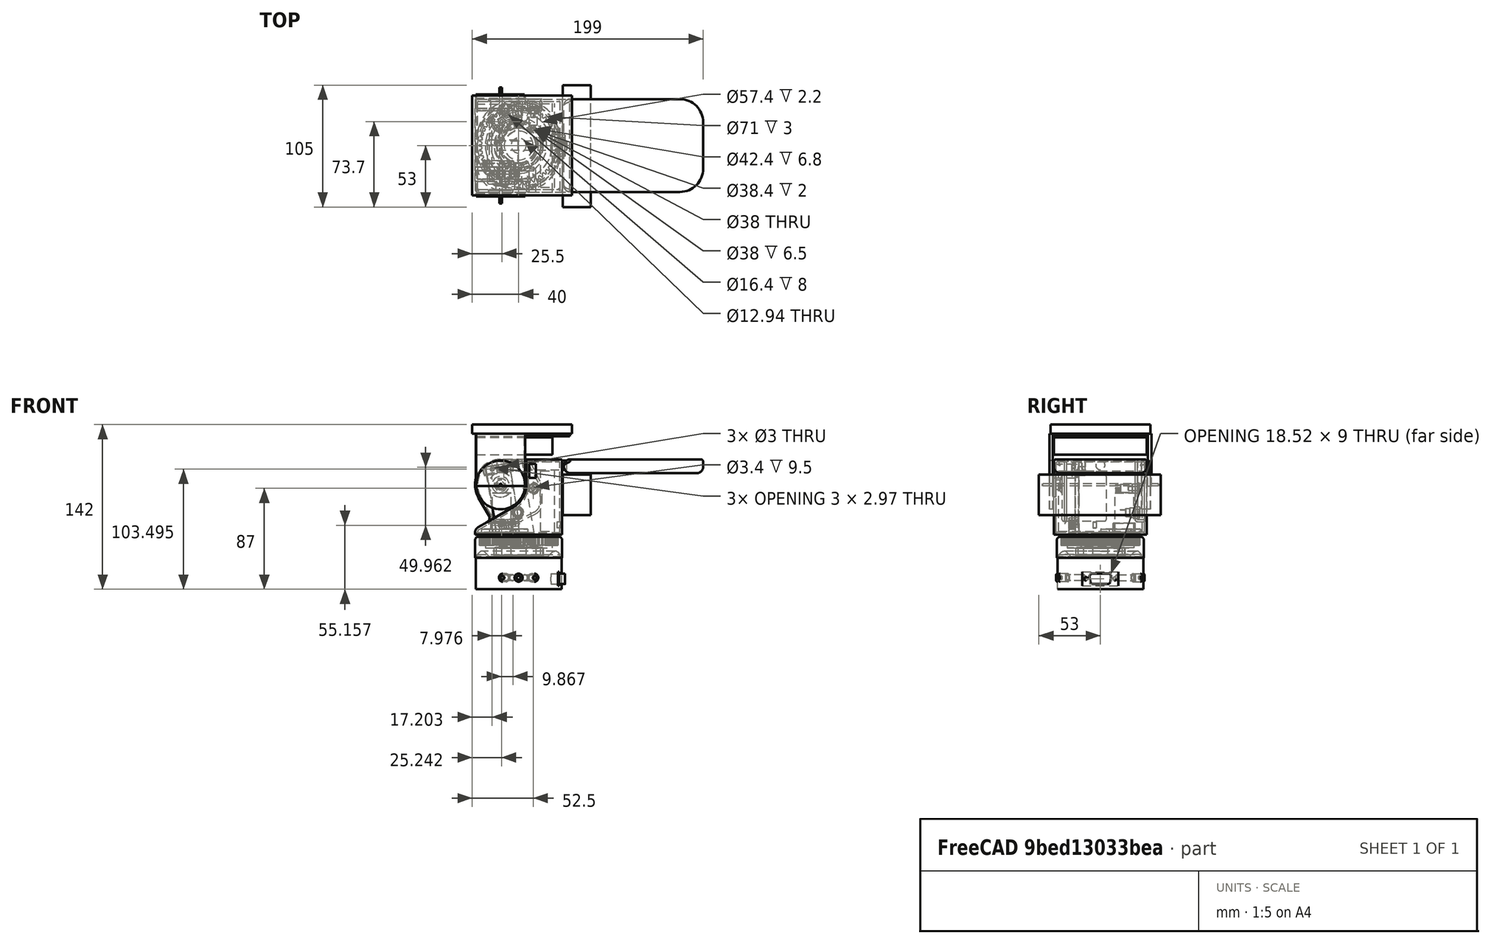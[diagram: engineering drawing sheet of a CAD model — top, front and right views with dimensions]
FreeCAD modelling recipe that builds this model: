
FCSTD DOCUMENT  (FreeCAD 0.16R6703 (Git))
Label: slewing_ring
License: CC-BY 3.0
LicenseURL: http://creativecommons.org/licenses/by/3.0/
objects: Part::Cylinder×23, Part::Fillet×23, Part::Cut×22, Part::Box×18, Part::Chamfer×8, Sketcher::SketchObject×7, Part::MultiFuse×7, Part::Sphere×4, Part::Extrusion×4, PartDesign::Fillet×4, Part::Cone×2, Part::FeaturePython×2, PartDesign::Revolution×1, Mesh::Feature×1, Part::Part2DObjectPython×1, Part::Revolution×1, Part::Feature×1, Part::Thickness×1, Part::Common×1
note: 131 computed .brp shape members not serialized (recipe doc carries the construction recipe); baked Part::Feature solids carry a one-line shape summary decoded from their .brp

FEATURE [Sketcher::SketchObject] Sketch  label="SlewingRingLowerBlankSketch"
  Placement = pos=(0,0,0) rot=(1,0,0;1.5708rad)
  sketch-geometry (13):
    g0: LineSegment StartX=-37.5 StartY=0 StartZ=0 EndX=-37.5 EndY=18.3 EndZ=0
    g1: LineSegment StartX=-37.5 StartY=18.3 StartZ=0 EndX=-28.7 EndY=18.3 EndZ=0
    g2: LineSegment StartX=-28.7 StartY=18.3 StartZ=0 EndX=-28.7 EndY=8.8 EndZ=0
    g3: LineSegment StartX=-28.7 StartY=8.8 StartZ=0 EndX=-21.2 EndY=8.8 EndZ=0
    g4: LineSegment StartX=-21.2 StartY=8.8 StartZ=0 EndX=-21.2 EndY=2 EndZ=0
    g5: LineSegment StartX=-21.2 StartY=2 StartZ=0 EndX=-19.2 EndY=2 EndZ=0
    g6: LineSegment StartX=-19.2 StartY=2 StartZ=0 EndX=-19.2 EndY=0 EndZ=0
    g7: LineSegment StartX=-37.5 StartY=0 StartZ=0 EndX=-35.5 EndY=0 EndZ=0
    g8: LineSegment StartX=-35.5 StartY=0 StartZ=0 EndX=-35.5 EndY=3 EndZ=0
    g9: LineSegment StartX=-35.5 StartY=3 StartZ=0 EndX=-33.4426 EndY=5.05736 EndZ=0
    g10: LineSegment StartX=-19.2 StartY=0 StartZ=0 EndX=-24.1426 EndY=0 EndZ=0
    g11: LineSegment StartX=-29.2 StartY=5.05736 StartZ=0 EndX=-24.1426 EndY=0 EndZ=0
    g12: ArcOfCircle CenterX=-31.3213 CenterY=2.93604 CenterZ=0 NormalX=0 NormalY=0 NormalZ=1 Radius=3 StartAngle=0.785398 EndAngle=2.35619
  constraints (38):
    c: Vertical(g0)
    c: Coincident(g0,g1)
    c: Horizontal(g1)
    c: Coincident(g1,g2)
    c: Vertical(g2)
    c: Coincident(g2,g3)
    c: Horizontal(g3)
    c: Coincident(g3,g4)
    c: Vertical(g4)
    c: Coincident(g4,g5)
    c: Coincident(g5,g6)
    c: DistanceY(g-1,g6) = 0
    c: Vertical(g6)
    c: Horizontal(g5)
    c: DistanceX(g4,g5) = 2
    c: DistanceY(g3,g4) = -6.8
    c: DistanceY(g5,g6) = -2
    c: DistanceX(g-1,g3) = -21.2
    c: DistanceX(g3,g2) = -7.5
    c: DistanceX(g-1,g0) = -37.5
    c: DistanceY(g2,g1) = 9.5
    c: DistanceY(g-1,g0) = 0
    c: Horizontal(g7)
    c: DistanceX(g7) = 2
    c: Coincident(g7,g0)
    c: Vertical(g8)
    c: DistanceY(g8) = 3
    c: Coincident(g8,g7)
    c: Angle(g9) = 0.785398
    c: Coincident(g9,g8)
    c: Horizontal(g10)
    c: Coincident(g10,g6)
    c: Coincident(g11,g10)
    c: Angle(g11) = -0.785398
    c: Distance(g2,g11) = 3
    c: Tangent(g9,g12)
    c: Tangent(g11,g12)
    c: Distance(g12,g9) = 3
FEATURE [Part::Cylinder] Cylinder  label="Cylinder21R"
  Angle = 360
  Height = 7
  Radius = 21
FEATURE [Part::Cylinder] Cylinder001  label="Cylinder19R"
  Angle = 360
  Height = 10
  Placement = pos=(0,0,-1.5) rot=(0,0,1;0rad)
  Radius = 19
FEATURE [Part::Cut] Cut  label="OuterRace"
  Base = -> Cylinder
  Tool = -> Cylinder001
FEATURE [Part::Cylinder] Cylinder002  label="Cylinder17R"
  Angle = 360
  Height = 7
  Radius = 17
FEATURE [Part::Cut] Cut001
  Base = -> Cylinder002
FEATURE [Part::Chamfer] Chamfer
  Base = -> Cut
  Edges = 1 edges r=0.5: [Edge1]
FEATURE [Part::Chamfer] Chamfer001
  Base = -> Chamfer
  Edges = 1 edges r=0.5: [Edge3]
FEATURE [Part::Chamfer] Chamfer002
  Base = -> Cut001
  Edges = 1 edges r=0.5: [Edge5]
FEATURE [Part::Chamfer] Chamfer003
  Base = -> Chamfer002
  Edges = 1 edges r=0.5: [Edge11]
FEATURE [Part::Chamfer] Chamfer004
  Base = -> Chamfer003
  Edges = 1 edges r=0.25: [Edge12]
FEATURE [Part::Chamfer] Chamfer005
  Base = -> Chamfer001
  Edges = 1 edges r=0.25: [Edge10]
FEATURE [Part::Sphere] Sphere  label="ballN"
  Angle1 = -90
  Angle2 = 90
  Angle3 = 360
  Placement = pos=(18,0,3.5) rot=(0,0,1;0rad)
  Radius = 2.5
FEATURE [Part::Sphere] Sphere3  label="ballS"
  Angle1 = -90
  Angle2 = 90
  Angle3 = 360
  Placement = pos=(-18,0,3.5) rot=(0,0,1;0rad)
  Radius = 2.5
FEATURE [Part::Sphere] Sphere004  label="ballW"
  Angle1 = -90
  Angle2 = 90
  Angle3 = 360
  Placement = pos=(0,18,3.5) rot=(0,0,1;0rad)
  Radius = 2.5
FEATURE [Part::Sphere] Sphere005  label="ballE"
  Angle1 = -90
  Angle2 = 90
  Angle3 = 360
  Placement = pos=(0,-18,3.5) rot=(0,0,1;0rad)
  Radius = 2.5
FEATURE [Part::MultiFuse] Fusion  label="ballrace30x42x7"
  Placement = pos=(0,0,2) rot=(0,0,1;0rad)
  Shapes = -> [Chamfer004,Chamfer005,Sphere,Sphere3,Sphere004,Sphere005]
FEATURE [Sketcher::SketchObject] Sketch001  label="SlewRingUpperSketch"
  Placement = pos=(0,0,0) rot=(0.57735,-0.57735,-0.57735;2.0944rad)
  sketch-geometry (8):
    g0: LineSegment StartX=-16.8 StartY=9.5 StartZ=0 EndX=-16.8 EndY=9 EndZ=0
    g1: LineSegment StartX=-16.8 StartY=9 StartZ=0 EndX=-14.8 EndY=9 EndZ=0
    g2: LineSegment StartX=-14.8 StartY=9 StartZ=0 EndX=-14.8 EndY=2.2 EndZ=0
    g3: LineSegment StartX=-14.8 StartY=2.2 StartZ=0 EndX=-6.47 EndY=2.2 EndZ=0
    g4: LineSegment StartX=-6.47 StartY=2.2 StartZ=0 EndX=-6.47 EndY=21.5 EndZ=0
    g5: LineSegment StartX=-6.47 StartY=21.5 StartZ=0 EndX=-12.47 EndY=21.5 EndZ=0
    g6: LineSegment StartX=-12.47 StartY=13.83 StartZ=0 EndX=-12.47 EndY=21.5 EndZ=0
    g7: LineSegment StartX=-16.8 StartY=9.5 StartZ=0 EndX=-12.47 EndY=13.83 EndZ=0
  constraints (24):
    c: Vertical(g0)
    c: Coincident(g0,g1)
    c: Coincident(g1,g2)
    c: Vertical(g2)
    c: Coincident(g2,g3)
    c: Horizontal(g3)
    c: Coincident(g3,g4)
    c: Vertical(g4)
    c: Horizontal(g1)
    c: DistanceX(g-1,g2) = -14.8
    c: DistanceY(g1,g2) = -6.8
    c: DistanceY(g-1,g3) = 2.2
    c: DistanceX(g1,g0) = -2
    c: DistanceX(g-1,g4) = -6.47
    c: Horizontal(g5)
    c: Vertical(g6)
    c: Coincident(g5,g4)
    c: DistanceY(g0,g0) = -0.5
    c: DistanceX(g6,g4) = 6
    c: Coincident(g7,g0)
    c: Angle(g7) = 0.785398
    c: Coincident(g7,g6)
    c: DistanceY(g5) = 21.5
    c: Coincident(g6,g5)
FEATURE [PartDesign::Revolution] Revolution  label="SlewingRingUpper"
  Angle = 360
  Axis = (0,0,1)
  Base = (0,0,0)
  Placement = pos=(0,0,0) rot=(0.57735,-0.57735,-0.57735;2.0944rad)
  ReferenceAxis = -> Sketch001 [V_Axis]
  Sketch = -> Sketch001
FEATURE [Part::Box] Box  label="ServoBody"
  Height = 38
  Length = 40.5
  Placement = pos=(-10.25,-10.25,0) rot=(0,0,1;0rad)
  Width = 20.5
FEATURE [Part::Cone] Cone  label="ServoBodyCone"
  Angle = 360
  Height = 2
  Placement = pos=(0,0,37.5) rot=(0,0,1;0rad)
  Radius1 = 8
  Radius2 = 5.5
FEATURE [Part::Cone] Cone001
  Angle = 360
  Height = 4
  Placement = pos=(0,0,39.75) rot=(0,0,1;0rad)
  Radius1 = 4.12
  Radius2 = 4.25
FEATURE [Part::Cylinder] Cylinder001001  label="shaft"
  Angle = 360
  Height = 4.5
  Placement = pos=(0,0,38.5) rot=(0,0,1;0rad)
  Radius = 3
FEATURE [Part::FeaturePython] Clone001  label="Screw_hole3"  # WARN: FeaturePython — macro-defined, semantics opaque (R4)
  Placement = pos=(34.5,5,26) rot=(0,0,1;0rad)
  Scale = (1,1,1)
FEATURE [Part::FeaturePython] Clone002  label="Screw_hole4"  # Draft clone (typed FeaturePython)
  Objects = -> [Clone001]
  Placement = pos=(34.5,-5,26) rot=(0,0,1;0rad)
  Scale = (1,1,1)
FEATURE [Part::Fillet] Fillet003  label="servo_lugs001"
  Edges = 1 edges r=1.5: [Edge24]
FEATURE [Part::Fillet] Fillet004  label="ServoBody001"
  Base = -> Box
  Edges = 12 edges r=1.5: [Edge1,Edge2,Edge3,Edge4,Edge5,Edge6,Edge7,Edge8,Edge9,Edge10,Edge11,Edge12]
FEATURE [Part::MultiFuse] Fusion001  label="TiltServo"
  Placement = pos=(-15.5,5,63) rot=(0.640191,0.54321,-0.54321;2.00277rad)
  Shapes = -> [Cone,Cone001,Cylinder001001,Fillet003,Fillet004]
FEATURE [Part::Cylinder] Cylinder002002  label="AntennaHingeRight"
  Angle = 360
  Height = 3
  Placement = pos=(-15.5,-41,63) rot=(1,0,0;1.5708rad)
  Radius = 21
FEATURE [Mesh::Feature] slipring
  Placement = pos=(0,0,4) rot=(0,1,0;3.14159rad)
FEATURE [Part::Cylinder] Cylinder004004
  Angle = 360
  Height = 11
  Placement = pos=(0,0,-2) rot=(0,0,1;0rad)
  Radius = 1.5
FEATURE [Part::Box] Box004
  Height = 15
  Length = 10
  Placement = pos=(1,-5,-4) rot=(0,0,1;0rad)
  Width = 10
FEATURE [Part::Cut] Cut003003
  Base = -> Cylinder004004
  Tool = -> Box004
FEATURE [Part::Cut] Cut001003  label="small_gear"
  Placement = pos=(-14.5,20.7,11.8) rot=(0,0,1;0.10472rad)
  Tool = -> Cut003003
FEATURE [Part::Part2DObjectPython] MainGear002  # Draft 2D object (typed FeaturePython)
  ExternalGear = false
  HighPrecision = true
  Modules = 1.27324
  NumberOfTeeth = 51
  PressureAngle = 20
FEATURE [Part::Extrusion] Extrude002  label="MainGearCutoutBlank"
  Base = -> MainGear002
  Dir = (0,0,8)
  Placement = pos=(0,0,11) rot=(0,0,1;0rad)
  Solid = true
FEATURE [Part::Revolution] Revolve  label="SlewingRingLowerRevolve"
  Angle = 360
  Axis = (0,0,1)
  Base = (0,0,0)
  Solid = false
  Source = -> Sketch
FEATURE [Part::Feature] Revolve_solid  label="SlewingRingLowerRevolve (Solid)"
  shape: bbox 75 x 75 x 18.3 mm, 13 faces (baked)
FEATURE [Part::Cut] Cut003004  label="SlewingRingLower01"
  Base = -> Revolve_solid
  Tool = -> Extrude002
FEATURE [Part::Box] Box005  label="UpperBase"
  Height = 2
  Length = 71
  Placement = pos=(-35.5,-38,20) rot=(0,0,1;0rad)
  Width = 76
FEATURE [Sketcher::SketchObject] Sketch004  label="antenna_mount_upper_sketch"
  Placement = pos=(-15.5,-44,63) rot=(1,0,0;1.5708rad)
  Support = -> Cylinder002002 [Face2]
  sketch-geometry (30):
    g0: GeomPoint [constr] X=-22 Y=0 Z=0
    g1: LineSegment StartX=-21 StartY=-37.5278 StartZ=0 EndX=11 EndY=-19.0526 EndZ=0
    g2: LineSegment StartX=-19.0526 StartY=-11 StartZ=0 EndX=-8.05255 EndY=-30.0526 EndZ=0
    g3: LineSegment [constr] StartX=-12.6401 StartY=15.1403 StartZ=0 EndX=7.09183 EndY=18.404 EndZ=0
    g4: LineSegment [constr] StartX=7.09183 StartY=18.404 StartZ=0 EndX=15.9038 EndY=-34.8722 EndZ=0
    g5: LineSegment [constr] StartX=15.9038 StartY=-34.8722 StartZ=0 EndX=-3.82815 EndY=-38.1359 EndZ=0
    g6: LineSegment [constr] StartX=-3.82815 StartY=-38.1359 StartZ=0 EndX=-12.6401 EndY=15.1403 EndZ=0
    g7: ArcOfCircle [constr] CenterX=0 CenterY=0 CenterZ=0 NormalX=0 NormalY=0 NormalZ=1 Radius=19.7231 StartAngle=1.20299 EndAngle=2.26644
    g8: GeomPoint [constr] X=-2.77413 Y=16.7721 Z=0
    g9: ArcOfCircle CenterX=0 CenterY=0 CenterZ=0 NormalX=0 NormalY=0 NormalZ=1 Radius=22 StartAngle=1.5708 EndAngle=3.66519
    g10: LineSegment StartX=-22 StartY=-39.2598 StartZ=0 EndX=-22 EndY=-43.2598 EndZ=0
    g11: ArcOfCircle CenterX=-20 CenterY=-39.2598 CenterZ=0 NormalX=0 NormalY=0 NormalZ=1 Radius=2 StartAngle=2.0944 EndAngle=3.14159
    g12: LineSegment StartX=-22 StartY=-43.2598 StartZ=0 EndX=53 EndY=-43.2598 EndZ=0
    g13: Circle [constr] CenterX=0 CenterY=0 CenterZ=0 NormalX=0 NormalY=0 NormalZ=1 Radius=10.5
    g14: ArcOfCircle CenterX=0 CenterY=0 CenterZ=0 NormalX=0 NormalY=0 NormalZ=1 Radius=22 StartAngle=5.23599 EndAngle=6.28319
    g15: LineSegment StartX=22 StartY=9e-12 StartZ=0 EndX=22 EndY=22 EndZ=0
    g16: Circle [constr] CenterX=19.5352 CenterY=-20.0593 CenterZ=0 NormalX=0 NormalY=0 NormalZ=1 Radius=6
    g17: Circle [constr] CenterX=26.1383 CenterY=-10.0394 CenterZ=0 NormalX=0 NormalY=0 NormalZ=1 Radius=6
    g18: LineSegment StartX=22 StartY=10 StartZ=0 EndX=59 EndY=10 EndZ=0
    g19: LineSegment StartX=25 StartY=7 StartZ=0 EndX=31.5 EndY=7 EndZ=0
    g20: LineSegment StartX=31.5 StartY=7 StartZ=0 EndX=31.5 EndY=-5.5 EndZ=0
    g21: LineSegment StartX=31.5 StartY=-5.5 StartZ=0 EndX=25 EndY=-5.5 EndZ=0
    g22: LineSegment StartX=25 StartY=-5.5 StartZ=0 EndX=25 EndY=7 EndZ=0
    g23: LineSegment StartX=31.1483 StartY=-13.3409 StartZ=0 EndX=24.5452 EndY=-23.3608 EndZ=0
    g24: Circle CenterX=-8.05255 CenterY=-30.0526 CenterZ=0 NormalX=0 NormalY=0 NormalZ=1 Radius=2.84871
    g25: ArcOfCircle CenterX=9.59993 CenterY=-26.7891 CenterZ=0 NormalX=0 NormalY=0 NormalZ=1 Radius=6 StartAngle=0.595371 EndAngle=2.0944
    g26: ArcOfCircle CenterX=31 CenterY=4.15092 CenterZ=0 NormalX=0 NormalY=0 NormalZ=1 Radius=9 StartAngle=3.14159 EndAngle=4.38232
    g27: LineSegment StartX=-2e-12 StartY=22 StartZ=0 EndX=59 EndY=22 EndZ=0
    g28: LineSegment StartX=53 StartY=-43.2598 StartZ=0 EndX=53 EndY=10 EndZ=0
    g29: ArcOfCircle CenterX=59 CenterY=16 CenterZ=0 NormalX=0 NormalY=0 NormalZ=1 Radius=6 StartAngle=4.71239 EndAngle=7.85398
  constraints (92):
    c: Distance(g-1,g0) = 22
    c: DistanceY(g-1,g0) = 0
    c: Perpendicular(g2,g1)
    c: Coincident(g3,g4)
    c: Coincident(g4,g5)
    c: Coincident(g5,g6)
    c: Coincident(g6,g3)
    c: Distance(g4,g5) = 20
    c: Distance(g3,g4) = 54
    c: Perpendicular(g3,g6)
    c: Perpendicular(g6,g5)
    c: Perpendicular(g5,g4)
    c: Coincident(g7,g3)
    c: Coincident(g7,g3)
    c: PointOnObject(g8,g3)
    c: Distance(g8,g3) = 10
    c: Distance(g7,g8) = 17
    c: Coincident(g7,g-1)
    c: Radius(g9) = 22
    c: Coincident(g9,g-1)
    c: Coincident(g9,g2)
    c: Tangent(g2,g9)
    c: Tangent(g1,g9)
    c: Vertical(g10)
    c: Tangent(g1,g11)
    c: Tangent(g10,g11)
    c: DistanceX(g-1,g10) = -22
    c: Radius(g11) = 2
    c: DistanceY(g10) = -4
    c: Horizontal(g12)
    c: Coincident(g12,g10)
    c: Distance(g12) = 75
    c: Angle(g1) = 0.523599
    c: Radius(g13) = 10.5
    c: Coincident(g13,g-1)
    c: Coincident(g14,g-1)
    c: Radius(g14) = 22
    c: Vertical(g15)
    c: Coincident(g14,g15)
    c: Radius(g16) = 6
    c: Radius(g17) = 6
    c: Horizontal(g18)
    c: PointOnObject(g18,g15)
    c: Tangent(g16,g4)
    c: Tangent(g16,g14)
    c: Tangent(g17,g16)
    c: Tangent(g17,g14)
    c: DistanceY(g-1,g14) = 0
    c: Coincident(g19,g20)
    c: Coincident(g20,g21)
    c: Coincident(g21,g22)
    c: Coincident(g22,g19)
    c: DistanceX(g19,g19) = 6.5
    c: DistanceY(g19,g20) = -12.5
    c: Perpendicular(g21,g22)
    c: Perpendicular(g20,g19)
    c: Perpendicular(g22,g19)
    c: Vertical(g22)
    c: DistanceX(g19,g14) = -3
    c: DistanceY(g18,g19) = -3
    c: PointOnObject(g23,g16)
    c: PointOnObject(g23,g17)
    c: Coincident(g1,g14)
    c: Coincident(g24,g2)
    c: PointOnObject(g2,g1)
    c: Tangent(g24,g6)
    c: Radius(g24) = 2.84871
    c: Tangent(g23,g16)
    c: Tangent(g23,g17)
    c: PointOnObject(g25,g16)
    c: PointOnObject(g25,g1)
    c: Tangent(g25,g1)
    c: Tangent(g25,g16)
    c: PointOnObject(g26,g17)
    c: PointOnObject(g26,g15)
    c: Tangent(g26,g17)
    c: Tangent(g26,g15)
    c: Radius(g25) = 6
    c: Radius(g26) = 9
    c: Horizontal(g27)
    c: Coincident(g27,g9)
    c: Vertical(g28)
    c: Coincident(g28,g12)
    c: PointOnObject(g28,g18)
    c: DistanceX(g29,g28) = -6
    c: DistanceY(g28,g29) = 6
    c: Coincident(g29,g27)
    c: Coincident(g18,g29)
    c: Tangent(g29,g27)
    c: Tangent(g29,g18)
    c: DistanceX(g-1,g9) = 0
    c: PointOnObject(g15,g27)
FEATURE [Part::Fillet] Fillet007  label="SlewRingLower"
  Base = -> Cut003004
  Edges = 1 edges r=3: [Edge1235]
FEATURE [Part::Cylinder] Cylinder004006  label="tilt_axis_cylinder"
  Angle = 360
  Height = 100
  Placement = pos=(-15.5,50,63) rot=(1,0,0;1.5708rad)
  Radius = 1
FEATURE [Part::Cut] Cut006  label="PanMotorTopBracket"
  Placement = pos=(-14.5,20.7,22) rot=(0,0,1;2.19912rad)
FEATURE [Part::Cylinder] Cylinder001006  label="Body001"
  Angle = 360
  Height = 4.6
  Placement = pos=(0,0,-4.5) rot=(0,0,1;0rad)
  Radius = 4
FEATURE [Part::Box] Box001001004  label="contact003"
  Height = 5.1
  Length = 1
  Placement = pos=(-0.5,2.5,-13) rot=(0,0,1;0rad)
  Width = 0.2
FEATURE [Part::Cylinder] Cylinder002007
  Angle = 360
  Height = 8.5
  Placement = pos=(0,0,-8) rot=(0,0,1;0rad)
  Radius = 3.4
FEATURE [Part::Box] Box001001005  label="contact004"
  Height = 5.1
  Length = 1
  Placement = pos=(-0.5,-2.5,-13) rot=(0,0,1;0rad)
  Width = 0.2
FEATURE [Part::Cylinder] Cylinder004009  label="Bezel002"
  Angle = 360
  Height = 4
  Radius = 5
FEATURE [Part::Chamfer] Chamfer008
  Base = -> Cylinder004009
  Edges = 1 edges r=0.5: [Edge1]
FEATURE [Part::MultiFuse] Fusion005  label="power_connector_blank"
  Shapes = -> [Cylinder001006,Box001001004,Cylinder002007,Box001001005,Chamfer008]
FEATURE [Part::Cylinder] Cylinder003003  label="hole001"
  Angle = 360
  Height = 10
  Radius = 2.85
FEATURE [Part::Cut] Cut003009  label="PowerConnector"
  Base = -> Fusion005
  Placement = pos=(-0.7,30,39.2) rot=(-1,0,0;1.5708rad)
  Tool = -> Cylinder003003
FEATURE [Sketcher::SketchObject] Sketch004001  label="upper_case_left_basic_extrusion_sketch"
  Placement = pos=(-15.5,-40,63) rot=(1,0,0;1.5708rad)
  sketch-geometry (28):
    g0: GeomPoint [constr] X=-22 Y=0 Z=0
    g1: LineSegment [constr] StartX=-21 StartY=-37.5278 StartZ=0 EndX=11 EndY=-19.0526 EndZ=0
    g2: LineSegment StartX=-19.0526 StartY=-11 StartZ=0 EndX=-8.05255 EndY=-30.0526 EndZ=0
    g3: LineSegment [constr] StartX=-12.6401 StartY=15.1403 StartZ=0 EndX=7.09183 EndY=18.404 EndZ=0
    g4: LineSegment [constr] StartX=7.09183 StartY=18.404 StartZ=0 EndX=15.9038 EndY=-34.8722 EndZ=0
    g5: LineSegment [constr] StartX=15.9038 StartY=-34.8722 StartZ=0 EndX=-3.82815 EndY=-38.1359 EndZ=0
    g6: LineSegment [constr] StartX=-3.82815 StartY=-38.1359 StartZ=0 EndX=-12.6401 EndY=15.1403 EndZ=0
    g7: ArcOfCircle [constr] CenterX=0 CenterY=0 CenterZ=0 NormalX=0 NormalY=0 NormalZ=1 Radius=19.7231 StartAngle=1.20299 EndAngle=2.26644
    g8: GeomPoint [constr] X=-2.77413 Y=16.7721 Z=0
    g9: ArcOfCircle CenterX=0 CenterY=0 CenterZ=0 NormalX=0 NormalY=0 NormalZ=1 Radius=22 StartAngle=1.5708 EndAngle=3.66519
    g10: LineSegment StartX=-22 StartY=-39.2598 StartZ=0 EndX=-22 EndY=-43.2598 EndZ=0
    g11: ArcOfCircle CenterX=-20 CenterY=-39.2598 CenterZ=0 NormalX=0 NormalY=0 NormalZ=1 Radius=2 StartAngle=2.0944 EndAngle=3.14159
    g12: LineSegment StartX=-22 StartY=-43.2598 StartZ=0 EndX=53 EndY=-43.2598 EndZ=0
    g13: ArcOfCircle [constr] CenterX=0 CenterY=0 CenterZ=0 NormalX=0 NormalY=0 NormalZ=1 Radius=22 StartAngle=5.23599 EndAngle=6.28319
    g14: LineSegment [constr] StartX=22 StartY=9e-12 StartZ=0 EndX=22 EndY=22 EndZ=0
    g15: Circle [constr] CenterX=19.5352 CenterY=-20.0593 CenterZ=0 NormalX=0 NormalY=0 NormalZ=1 Radius=6
    g16: Circle [constr] CenterX=26.1383 CenterY=-10.0394 CenterZ=0 NormalX=0 NormalY=0 NormalZ=1 Radius=6
    g17: LineSegment [constr] StartX=25 StartY=7 StartZ=0 EndX=31.5 EndY=7 EndZ=0
    g18: LineSegment [constr] StartX=31.5 StartY=7 StartZ=0 EndX=31.5 EndY=-5.5 EndZ=0
    g19: LineSegment [constr] StartX=31.5 StartY=-5.5 StartZ=0 EndX=25 EndY=-5.5 EndZ=0
    g20: LineSegment [constr] StartX=25 StartY=-5.5 StartZ=0 EndX=25 EndY=7 EndZ=0
    g21: LineSegment [constr] StartX=31.1483 StartY=-13.3409 StartZ=0 EndX=24.5452 EndY=-23.3608 EndZ=0
    g22: Circle [constr] CenterX=-8.05255 CenterY=-30.0526 CenterZ=0 NormalX=0 NormalY=0 NormalZ=1 Radius=2.84871
    g23: ArcOfCircle [constr] CenterX=9.59993 CenterY=-26.7891 CenterZ=0 NormalX=0 NormalY=0 NormalZ=1 Radius=6 StartAngle=0.595371 EndAngle=2.0944
    g24: ArcOfCircle [constr] CenterX=31 CenterY=4.15092 CenterZ=0 NormalX=0 NormalY=0 NormalZ=1 Radius=9 StartAngle=3.14159 EndAngle=4.38232
    g25: LineSegment StartX=-2e-12 StartY=22 StartZ=0 EndX=53 EndY=22 EndZ=0
    g26: LineSegment StartX=53 StartY=-43.2598 StartZ=0 EndX=53 EndY=22 EndZ=0
    g27: LineSegment StartX=-21 StartY=-37.5278 StartZ=0 EndX=-8.05255 EndY=-30.0526 EndZ=0
  constraints (84):
    c: Distance(g-1,g0) = 22
    c: DistanceY(g-1,g0) = 0
    c: Perpendicular(g2,g1)
    c: Coincident(g3,g4)
    c: Coincident(g4,g5)
    c: Coincident(g5,g6)
    c: Coincident(g6,g3)
    c: Distance(g4,g5) = 20
    c: Distance(g3,g4) = 54
    c: Perpendicular(g3,g6)
    c: Perpendicular(g6,g5)
    c: Perpendicular(g5,g4)
    c: Coincident(g7,g3)
    c: Coincident(g7,g3)
    c: PointOnObject(g8,g3)
    c: Distance(g8,g3) = 10
    c: Distance(g7,g8) = 17
    c: Coincident(g7,g-1)
    c: Radius(g9) = 22
    c: Coincident(g9,g-1)
    c: Coincident(g9,g2)
    c: Tangent(g2,g9)
    c: Tangent(g1,g9)
    c: Vertical(g10)
    c: Tangent(g1,g11)
    c: Tangent(g10,g11)
    c: DistanceX(g-1,g10) = -22
    c: Radius(g11) = 2
    c: DistanceY(g10) = -4
    c: Horizontal(g12)
    c: Coincident(g12,g10)
    c: Distance(g12) = 75
    c: Angle(g1) = 0.523599
    c: Coincident(g13,g-1)
    c: Radius(g13) = 22
    c: Vertical(g14)
    c: Coincident(g13,g14)
    c: Radius(g15) = 6
    c: Radius(g16) = 6
    c: Tangent(g15,g4)
    c: Tangent(g15,g13)
    c: Tangent(g16,g15)
    c: Tangent(g16,g13)
    c: DistanceY(g-1,g13) = 0
    c: Coincident(g17,g18)
    c: Coincident(g18,g19)
    c: Coincident(g19,g20)
    c: Coincident(g20,g17)
    c: DistanceX(g17,g17) = 6.5
    c: DistanceY(g17,g18) = -12.5
    c: Perpendicular(g19,g20)
    c: Perpendicular(g18,g17)
    c: Perpendicular(g20,g17)
    c: Vertical(g20)
    c: DistanceX(g17,g13) = -3
    c: PointOnObject(g21,g15)
    c: PointOnObject(g21,g16)
    c: Coincident(g1,g13)
    c: Coincident(g22,g2)
    c: PointOnObject(g2,g1)
    c: Tangent(g22,g6)
    c: Radius(g22) = 2.84871
    c: Tangent(g21,g15)
    c: Tangent(g21,g16)
    c: PointOnObject(g23,g15)
    c: PointOnObject(g23,g1)
    c: Tangent(g23,g1)
    c: Tangent(g23,g15)
    c: PointOnObject(g24,g16)
    c: PointOnObject(g24,g14)
    c: Tangent(g24,g16)
    c: Tangent(g24,g14)
    c: Radius(g23) = 6
    c: Radius(g24) = 9
    c: Horizontal(g25)
    c: Coincident(g25,g9)
    c: Vertical(g26)
    c: Coincident(g26,g12)
    c: DistanceX(g-1,g9) = 0
    c: PointOnObject(g14,g25)
    c: Coincident(g27,g2)
    c: Coincident(g27,g1)
    c: Coincident(g25,g26)
    c: DistanceY(g17) = 7
FEATURE [Sketcher::SketchObject] Sketch004001001  label="upper_case_left_antenna_mount_pocket_sketch"
  Placement = pos=(-15.5,-31,63) rot=(1,0,0;1.5708rad)
  sketch-geometry (12):
    g0: LineSegment [constr] StartX=-12.6525 StartY=15.1299 StartZ=0 EndX=7.07676 EndY=18.4098 EndZ=0
    g1: LineSegment [constr] StartX=7.07676 StartY=18.4098 StartZ=0 EndX=15.9323 EndY=-34.8592 EndZ=0
    g2: LineSegment [constr] StartX=15.9323 StartY=-34.8592 StartZ=0 EndX=-3.79693 EndY=-38.139 EndZ=0
    g3: LineSegment [constr] StartX=-3.79693 StartY=-38.139 StartZ=0 EndX=-12.6525 EndY=15.1299 EndZ=0
    g4: ArcOfCircle [constr] CenterX=0 CenterY=0 CenterZ=0 NormalX=0 NormalY=0 NormalZ=1 Radius=19.7231 StartAngle=1.20381 EndAngle=2.26726
    g5: GeomPoint [constr] X=-2.78786 Y=16.7698 Z=0
    g6: ArcOfCircle CenterX=0 CenterY=0 CenterZ=0 NormalX=0 NormalY=0 NormalZ=1 Radius=23 StartAngle=1.5708 EndAngle=3.221
    g7: ArcOfCircle CenterX=0 CenterY=0 CenterZ=0 NormalX=0 NormalY=0 NormalZ=1 Radius=22 StartAngle=5.23599 EndAngle=6.28319
    g8: LineSegment StartX=22 StartY=0 StartZ=0 EndX=22 EndY=23 EndZ=0
    g9: LineSegment StartX=22 StartY=23 StartZ=0 EndX=0 EndY=23 EndZ=0
    g10: LineSegment StartX=-20.1265 StartY=-37.0235 StartZ=0 EndX=11 EndY=-19.0525 EndZ=0
    g11: LineSegment StartX=-22.9275 StartY=-1.82454 StartZ=0 EndX=-20.1265 EndY=-37.0235 EndZ=0
  constraints (34):
    c: Coincident(g0,g1)
    c: Coincident(g1,g2)
    c: Coincident(g2,g3)
    c: Coincident(g3,g0)
    c: Distance(g1,g2) = 20
    c: Distance(g0,g1) = 54
    c: Perpendicular(g0,g3)
    c: Perpendicular(g3,g2)
    c: Perpendicular(g2,g1)
    c: Coincident(g4,g0)
    c: Coincident(g4,g0)
    c: PointOnObject(g5,g0)
    c: Distance(g5,g0) = 10
    c: Distance(g4,g5) = 17
    c: Coincident(g4,g-1)
    c: Radius(g6) = 23
    c: Coincident(g6,g-1)
    c: Coincident(g7,g-1)
    c: Radius(g7) = 22
    c: Vertical(g8)
    c: Coincident(g7,g8)
    c: DistanceY(g-1,g7) = 0
    c: DistanceX(g-1,g6) = 0
    c: DistanceY(g8,g6) = 0
    c: Coincident(g9,g8)
    c: Coincident(g9,g6)
    c: Coincident(g10,g7)
    c: Tangent(g7,g10)
    c: Angle(g10) = 0.523599
    c: Coincident(g11,g6)
    c: Tangent(g11,g6)
    c: DistanceX(g6) = -22.9275
    c: DistanceX(g1) = 15.9323
    c: Coincident(g11,g10)
FEATURE [Sketcher::SketchObject] Sketch004001002  label="upper_case_right_antenna_mount_pocket_sketch"
  Placement = pos=(-15.5,32,63) rot=(1,0,0;1.5708rad)
  sketch-geometry (15):
    g0: ArcOfCircle CenterX=0 CenterY=0 CenterZ=0 NormalX=0 NormalY=0 NormalZ=1 Radius=22 StartAngle=1.5708 EndAngle=3.1416
    g1: LineSegment StartX=22 StartY=22 StartZ=0 EndX=0 EndY=22 EndZ=0
    g2: LineSegment StartX=-22 StartY=-29.7621 StartZ=0 EndX=14.811 EndY=-29.7621 EndZ=0
    g3: LineSegment StartX=33.2147 StartY=0.0557451 StartZ=0 EndX=22 EndY=22 EndZ=0
    g4: ArcOfCircle [constr] CenterX=0 CenterY=0 CenterZ=0 NormalX=0 NormalY=0 NormalZ=1 Radius=28 StartAngle=5.26977 EndAngle=6.18752
    g5: ArcOfCircle CenterX=14.811 CenterY=-23.7621 CenterZ=0 NormalX=0 NormalY=0 NormalZ=1 Radius=6 StartAngle=4.71239 EndAngle=5.17409
    g6: GeomPoint [constr] X=24.6541 Y=-15.2701 Z=0
    g7: ArcOfCircle CenterX=24.6541 CenterY=-15.2701 CenterZ=0 NormalX=0 NormalY=0 NormalZ=1 Radius=9.21791 StartAngle=5.17409 EndAngle=6.28319
    g8: LineSegment StartX=17.4838 StartY=-29.1338 StartZ=0 EndX=28.7604 EndY=-23.5229 EndZ=0
    g9: ArcOfCircle CenterX=27.872 CenterY=-2.67468 CenterZ=0 NormalX=0 NormalY=0 NormalZ=1 Radius=6 StartAngle=2.064e-06 EndAngle=0.472451
    g10: LineSegment StartX=33.872 StartY=-2.67467 StartZ=0 EndX=33.872 EndY=-15.2701 EndZ=0
    g11: Circle [constr] CenterX=27.872 CenterY=-2.67468 CenterZ=0 NormalX=0 NormalY=0 NormalZ=1 Radius=5.5
    g12: Circle [constr] CenterX=14.811 CenterY=-23.7621 CenterZ=0 NormalX=0 NormalY=0 NormalZ=1 Radius=5.5
    g13: Circle [constr] CenterX=24.6541 CenterY=-15.2701 CenterZ=0 NormalX=0 NormalY=0 NormalZ=1 Radius=6
    g14: LineSegment StartX=-22 StartY=-29.7621 StartZ=0 EndX=-22 EndY=-5.40922e-05 EndZ=0
  constraints (42):
    c: Radius(g0) = 22
    c: Coincident(g0,g-1)
    c: DistanceX(g-1,g0) = 0
    c: Coincident(g1,g0)
    c: Horizontal(g1)
    c: DistanceX(g1) = 22
    c: Coincident(g3,g1)
    c: Coincident(g4,g-1)
    c: Radius(g4) = 28
    c: DistanceX(g4) = 14.811
    c: Coincident(g5,g4)
    c: DistanceX(g6) = 24.6541
    c: DistanceY(g6) = -15.2701
    c: Coincident(g7,g6)
    c: Coincident(g8,g5)
    c: Tangent(g8,g5)
    c: Coincident(g8,g7)
    c: Tangent(g7,g8)
    c: Coincident(g9,g4)
    c: Coincident(g7,g10)
    c: Tangent(g10,g7)
    c: Coincident(g10,g9)
    c: Tangent(g10,g9)
    c: Radius(g9) = 6
    c: Radius(g5) = 6
    c: Radius(g7) = 9.21791
    c: Distance(g4,g6) = 13
    c: Radius(g11) = 5.5
    c: Coincident(g11,g4)
    c: Radius(g12) = 5.5
    c: Coincident(g12,g4)
    c: Radius(g13) = 6
    c: Coincident(g13,g6)
    c: Coincident(g2,g5)
    c: Tangent(g5,g2)
    c: Coincident(g9,g3)
    c: Tangent(g9,g3)
    c: Horizontal(g2)
    c: Coincident(g14,g0)
    c: Coincident(g2,g14)
    c: Tangent(g14,g0)
    c: Vertical(g14)
FEATURE [Part::Cylinder] Cylinder004010  label="MagGpsShelfRetSlide"
  Angle = 360
  Height = 60
  Placement = pos=(-18.5,0,80) rot=(0,1,0;1.5708rad)
  Radius = 4
FEATURE [Part::Cylinder] Cylinder001008  label="motor_shaft"
  Angle = 360
  Height = 8
  Placement = pos=(0,0,-8) rot=(0,0,1;0rad)
  Radius = 1.5
FEATURE [Part::Cylinder] Cylinder002009  label="bearing"
  Angle = 360
  Height = 2.5
  Placement = pos=(0,0,-2) rot=(0,0,1;0rad)
  Radius = 3
FEATURE [Part::Cylinder] Cylinder003004
  Angle = 360
  Height = 8.5
  Placement = pos=(5.5,0,-8) rot=(0,0,1;0rad)
  Radius = 1
FEATURE [Part::Cylinder] Cylinder004012
  Angle = 360
  Height = 8.5
  Placement = pos=(-5.5,0,-8) rot=(0,0,1;0rad)
  Radius = 1
FEATURE [Part::Cut] Cut003010
  Tool = -> Cylinder003004
FEATURE [Part::Cut] Cut001005
  Base = -> Cut003010
  Tool = -> Cylinder004012
FEATURE [Part::MultiFuse] Fusion006  label="16mmGearMotor"
  Placement = pos=(-14.5,20.7,22) rot=(0,0,1;0.785397rad)
  Shapes = -> [Cylinder001008,Cylinder002009,Cut001005]
FEATURE [Sketcher::SketchObject] Sketch004001003  label="upper_case_right_basic_extrusion_sketch"
  Placement = pos=(-15.5,40,63) rot=(1,0,0;1.5708rad)
  sketch-geometry (17):
    g0: GeomPoint [constr] X=-22 Y=0 Z=0
    g1: LineSegment StartX=-19.0526 StartY=-11 StartZ=0 EndX=-10.0526 EndY=-26.5885 EndZ=0
    g2: LineSegment [constr] StartX=-12.5188 StartY=15.2407 StartZ=0 EndX=7.23855 EndY=18.3468 EndZ=0
    g3: LineSegment [constr] StartX=7.23855 StartY=18.3468 StartZ=0 EndX=15.6248 EndY=-34.9981 EndZ=0
    g4: LineSegment [constr] StartX=15.6248 StartY=-34.9981 StartZ=0 EndX=-4.13252 EndY=-38.1041 EndZ=0
    g5: LineSegment [constr] StartX=-4.13252 StartY=-38.1041 StartZ=0 EndX=-12.5188 EndY=15.2407 EndZ=0
    g6: ArcOfCircle [constr] CenterX=0 CenterY=0 CenterZ=0 NormalX=0 NormalY=0 NormalZ=1 Radius=19.7231 StartAngle=1.195 EndAngle=2.25845
    g7: GeomPoint [constr] X=-2.64012 Y=16.7937 Z=0
    g8: ArcOfCircle CenterX=0 CenterY=0 CenterZ=0 NormalX=0 NormalY=0 NormalZ=1 Radius=22 StartAngle=1.5708 EndAngle=3.66519
    g9: LineSegment StartX=-22 StartY=-40.9919 StartZ=0 EndX=-22 EndY=-42.9919 EndZ=0
    g10: ArcOfCircle CenterX=-17 CenterY=-40.9919 CenterZ=0 NormalX=0 NormalY=0 NormalZ=1 Radius=5 StartAngle=2.0944 EndAngle=3.14159
    g11: LineSegment StartX=-22 StartY=-42.9919 StartZ=0 EndX=53 EndY=-42.9919 EndZ=0
    g12: Circle [constr] CenterX=-8.36785 CenterY=-29.5065 CenterZ=0 NormalX=0 NormalY=0 NormalZ=1 Radius=2.84871
    g13: LineSegment StartX=0 StartY=22 StartZ=0 EndX=53 EndY=22 EndZ=0
    g14: LineSegment StartX=53 StartY=-42.9919 StartZ=0 EndX=53 EndY=22 EndZ=0
    g15: LineSegment StartX=-19.5 StartY=-36.6618 StartZ=0 EndX=-11.5167 EndY=-32.0526 EndZ=0
    g16: ArcOfCircle CenterX=-13.5167 CenterY=-28.5885 CenterZ=0 NormalX=0 NormalY=0 NormalZ=1 Radius=4 StartAngle=5.23599 EndAngle=6.80678
  constraints (45):
    c: DistanceY(g-1,g0) = 0
    c: Coincident(g2,g3)
    c: Coincident(g3,g4)
    c: Coincident(g4,g5)
    c: Coincident(g5,g2)
    c: Distance(g3,g4) = 20
    c: Distance(g2,g3) = 54
    c: Perpendicular(g2,g5)
    c: Perpendicular(g5,g4)
    c: Perpendicular(g4,g3)
    c: Coincident(g6,g2)
    c: Coincident(g6,g2)
    c: PointOnObject(g7,g2)
    c: Distance(g7,g2) = 10
    c: Distance(g6,g7) = 17
    c: Coincident(g6,g-1)
    c: Radius(g8) = 22
    c: Coincident(g8,g-1)
    c: Coincident(g8,g1)
    c: Tangent(g1,g8)
    c: Vertical(g9)
    c: Tangent(g15,g10)
    c: Tangent(g9,g10)
    c: DistanceX(g-1,g9) = -22
    c: Radius(g10) = 5
    c: DistanceY(g9) = -2
    c: Horizontal(g11)
    c: Coincident(g11,g9)
    c: Distance(g11) = 75
    c: Tangent(g12,g5)
    c: Radius(g12) = 2.84871
    c: Horizontal(g13)
    c: Coincident(g13,g8)
    c: Vertical(g14)
    c: Coincident(g14,g11)
    c: DistanceX(g-1,g8) = 0
    c: DistanceX(g13,g14) = 0
    c: Coincident(g14,g13)
    c: Perpendicular(g1,g15)
    c: Angle(g15) = 0.523599
    c: Tangent(g1,g16)
    c: Tangent(g15,g16)
    c: Angle(g15) = 0.523599
    c: Radius(g16) = 4
    c: Tangent(g15,g8)
FEATURE [Part::Box] Box001001006  label="BalanceChargerPwrSocket"
  Height = 12
  Length = 6
  Placement = pos=(9,-40,69) rot=(0,0,1;0rad)
  Width = 20
FEATURE [Part::Extrusion] Extrude  label="UpperCaseExtrude01"
  Base = -> Sketch004001003
  Dir = (0,-80,0)
  Solid = true
FEATURE [Part::Extrusion] Extrude003  label="upper_case_right_pocket"
  Base = -> Sketch004001002
  Dir = (0,11,0)
  Solid = true
FEATURE [Part::Extrusion] Extrude004  label="upper_case_left_pocket"
  Base = -> Sketch004001001
  Dir = (0,-12,0)
  Solid = true
FEATURE [Part::Cut] Cut003011  label="UpperCase02"
  Base = -> Extrude
  Tool = -> Extrude004
FEATURE [Part::Cut] Cut003012  label="UpperCase03"
  Base = -> Cut003011
  Tool = -> Extrude003
FEATURE [Part::Thickness] Thickness  label="upper_case_shell"
  Faces = -> Cut003012 [Face3]
  Intersection = false
  Join = 0
  Mode = 0
  SelfIntersection = false
  Value = -2
FEATURE [Part::Fillet] Fillet008
  Base = -> Thickness
  Edges = 3 edges r=2: [Edge26,Edge27,Edge43]
FEATURE [Part::Fillet] Fillet009
  Base = -> Fillet008
  Edges = 3 edges r=2: [Edge17,Edge18,Edge52]
FEATURE [Part::Fillet] Fillet010  label="UpperCase01"
  Base = -> Fillet009
  Edges = 1 edges r=1: [Edge3]
FEATURE [Part::Cylinder] Cylinder004013  label="Bezel"
  Angle = 360
  Height = 1.5
  Radius = 5
FEATURE [Part::Cylinder] Cylinder001009  label="M8_threaded"
  Angle = 360
  Height = 4.6
  Placement = pos=(0,0,-4.5) rot=(0,0,1;0rad)
  Radius = 4
FEATURE [Part::Cylinder] Cylinder002010
  Angle = 360
  Height = 16
  Placement = pos=(0,0,-14.5) rot=(0,0,1;0rad)
  Radius = 3.5
FEATURE [Part::Box] Box001001007  label="Contact"
  Height = 4.6
  Length = 1.5
  Placement = pos=(-1,-3,-19) rot=(0,0,1;0rad)
  Width = 0.25
FEATURE [Part::Box] Box001001008  label="Contact001"
  Height = 4.6
  Length = 1.5
  Placement = pos=(-1,2,-19) rot=(0,0,1;0rad)
  Width = 0.25
FEATURE [Part::Box] Box001001  label="Contact002"
  Height = 4.6
  Length = 1.5
  Placement = pos=(2,-0.8,-19) rot=(0,0,1;1.5708rad)
  Width = 0.25
FEATURE [Part::Box] Box001002  label="Contact003"
  Height = 4.6
  Length = 1.5
  Placement = pos=(-2,-0.9,-19) rot=(0,0,1;1.5708rad)
  Width = 0.25
FEATURE [Part::Chamfer] Chamfer009
  Base = -> Cylinder004013
  Edges = 1 edges r=0.5: [Edge1]
FEATURE [Part::Cylinder] Cylinder003005  label="hole"
  Angle = 360
  Height = 10
  Placement = pos=(0,0,-8) rot=(0,0,1;0rad)
  Radius = 1.7
FEATURE [Part::MultiFuse] Fusion001002
  Shapes = -> [Cylinder001009,Cylinder002010,Box001001007,Box001001008,Box001001,Box001002,Chamfer009]
FEATURE [Part::Cut] Cut003013  label="4_way_jack_socket"
  Base = -> Fusion001002
  Placement = pos=(12.5,32,60) rot=(-1,0,0;1.5708rad)
  Tool = -> Cylinder003005
FEATURE [PartDesign::Fillet] Fillet011  label="UpperCase011"
  Base = -> Fillet009 [Edge151,Edge109,Edge108,Edge101,Edge149,Edge152,Edge153,Edge155,Edge156]
  Radius = 2
FEATURE [PartDesign::Fillet] Fillet012  label="UpperCase012"
  Base = -> Fillet010 [Edge94,Edge95,Edge96,Edge97,Edge98,Edge99,Edge100,Edge101,Edge45,Edge93,Edge102,Edge103,Edge104,Edge105]
  Radius = 1
FEATURE [PartDesign::Fillet] Fillet013
  Base = -> Fillet011 [Edge29,Edge40,Edge80,Edge44,Edge81,Edge49,Edge82,Edge83]
  Radius = 1
FEATURE [Part::Fillet] Fillet014
  Base = -> Fillet013
  Edges = 1 edges r=1: [Edge212]
FEATURE [Part::Fillet] Fillet015  label="UpperCase015"
  Base = -> Fillet014
  Edges = 1 edges r=1: [Edge38]
FEATURE [PartDesign::Fillet] Fillet016  label="UpperCase"
  Base = -> Fillet015 [Edge144,Edge145,Edge146,Edge148,Edge149,Edge150,Edge83,Edge151,Edge140,Edge152,Edge153,Edge154,Edge155,Edge156,Edge157]
  Radius = 1
FEATURE [Part::Box] Box001001009  label="PcbBox"
  Height = 52
  Length = 12
  Placement = pos=(19,-36,23) rot=(0,0,1;0rad)
  Width = 72
FEATURE [Part::MultiFuse] Fusion002001003
FEATURE [Part::MultiFuse] Fusion002001002  label="nut_trap_holes_subtract"
  Shapes = -> [Box004]
FEATURE [Part::Cut] Cut007001  label="ServoMount002"
  Base = -> Fusion002001003
  Placement = pos=(-15.5,10,63) rot=(0.640285,0.543005,-0.543305;2.00301rad)
  Tool = -> Fusion002001002
FEATURE [Part::Common] Common002  label="TiltServoMount"
  Base = -> Extrude
  Placement = pos=(0,1,0) rot=(0,0,1;0rad)
  Tool = -> Cut007001
FEATURE [Part::Cylinder] Cylinder004014  label="LowerCase"
  Angle = 360
  Height = 28
  Placement = pos=(0,0,-27) rot=(0,0,1;0rad)
  Radius = 37
FEATURE [Part::Cylinder] Cylinder001010  label="screw_hole2"
  Angle = 360
  Height = 10
  Placement = pos=(12.27,0,0) rot=(0,0,1;0rad)
  Radius = 1.5
FEATURE [Part::Cut] Cut007002
  Base = -> Fusion
  Tool = -> Cylinder
FEATURE [Part::Cut] Cut001006  label="DB9_connector"
  Base = -> Cut007002
  Placement = pos=(28,0,-18) rot=(0.57735,0.57735,0.57735;2.0944rad)
  Tool = -> Cylinder001010
FEATURE [Part::Cut] Cut007003001
  Base = -> Fusion
  Tool = -> Cylinder001
FEATURE [Part::Fillet] Fillet003002001  label="RCA_socket001"
  Base = -> Cut007003001
  Edges = 1 edges r=1: [Edge3]
  Placement = pos=(11,-28,-17) rot=(0.964231,0.187427,0.187427;1.60721rad)
FEATURE [Part::Cut] Cut007003002
  Base = -> Fusion
  Tool = -> Cylinder001
FEATURE [Part::Fillet] Fillet003002002  label="RCA_socket002"
  Base = -> Cut007003002
  Edges = 1 edges r=1: [Edge3]
  Placement = pos=(0,-30,-17) rot=(1,0,0;1.5708rad)
FEATURE [Part::Cut] Cut007003003
  Base = -> Fusion
  Tool = -> Cylinder001
FEATURE [Part::Fillet] Fillet003002003  label="RCA_socket003"
  Base = -> Cut007003003
  Edges = 1 edges r=1: [Edge3]
  Placement = pos=(-11,-28,-17) rot=(0.964231,-0.187427,-0.187427;1.60721rad)
FEATURE [Part::Cut] Cut007003004
  Base = -> Fusion
  Tool = -> Cylinder001
FEATURE [Part::Fillet] Fillet003002004  label="RCA_socket004"
  Base = -> Cut007003004
  Edges = 1 edges r=1: [Edge3]
  Placement = pos=(-11,28,-17) rot=(-0.136167,0.700521,0.700521;3.41229rad)
FEATURE [Part::Cut] Cut007003005
  Base = -> Fusion
  Tool = -> Cylinder001
FEATURE [Part::Fillet] Fillet003002005  label="RCA_socket005"
  Base = -> Cut007003005
  Edges = 1 edges r=1: [Edge3]
  Placement = pos=(0,30,-17) rot=(0,0.707107,0.707107;3.14159rad)
FEATURE [Part::Cut] Cut007003006
  Base = -> Fusion
  Tool = -> Cylinder001
FEATURE [Part::Fillet] Fillet003002006  label="RCA_socket006"
  Base = -> Cut007003006
  Edges = 1 edges r=1: [Edge3]
  Placement = pos=(11,28,-17) rot=(0.136167,0.700521,0.700521;2.87089rad)
FEATURE [Part::Cut] Cut007003
  Base = -> Fusion
  Tool = -> Cylinder001
FEATURE [Part::Cylinder] Cylinder002002001  label="AntennaHingeLeft"
  Angle = 360
  Height = 7.5
  Placement = pos=(-15.5,43,63) rot=(1,0,0;1.5708rad)
  Radius = 21
FEATURE [Part::Box] Box001001011  label="MagGPSShelf"
  Height = 12
  Length = 120
  Placement = pos=(39,-40,73) rot=(0,0,1;0rad)
  Width = 80
FEATURE [Part::Fillet] Fillet003002007
  Base = -> Box001001011
  Edges = 1 edges r=20: [Edge5]
FEATURE [Part::Fillet] Fillet003002008
  Base = -> Fillet003002007
  Edges = 1 edges r=20: [Edge3]
FEATURE [Part::Box] Box001001012  label="Battery"
  Height = 35
  Length = 24
  Placement = pos=(38,-53,37) rot=(0,0,1;0rad)
  Width = 105
FEATURE [Part::Fillet] Fillet003002009
  Base = -> Fillet003002008
  Edges = 1 edges r=6: [Edge16]
FEATURE [Part::Fillet] Fillet003002010
  Base = -> Fillet003002009
  Edges = 1 edges r=2: [Edge10]
FEATURE [Part::Fillet] Fillet003002011
  Base = -> Fillet003002010
  Edges = 1 edges r=5.5: [Edge19]
FEATURE [Part::Box] Box001001013  label="AntennaMount_left_leg"
  Height = 45
  Length = 42
  Placement = pos=(-36.5,-44,62) rot=(0,0,1;0rad)
  Width = 3
FEATURE [Part::Box] Box001001013001  label="AntennaMount_right_leg"
  Height = 45
  Length = 42
  Placement = pos=(-37,41,62) rot=(0,0,1;0rad)
  Width = 3
FEATURE [Part::Box] Box001001013002  label="AntennaMount"
  Height = 2
  Length = 80
  Placement = pos=(-36,-40,105) rot=(0,0,1;0rad)
  Width = 80
FEATURE [Part::Box] Box001001013003  label="Vrx"
  Height = 15
  Length = 65
  Placement = pos=(-36,-40,89) rot=(0,0,1;0rad)
  Width = 80
FEATURE [Part::Box] Box001001013004  label="Patch"
  Height = 8
  Length = 86
  Placement = pos=(-40,-43,107) rot=(0,0,1;0rad)
  Width = 86
FEATURE [Part::Fillet] Fillet003002012
  Base = -> Box005
  Edges = 1 edges r=20: [Edge1]
FEATURE [Part::Fillet] Fillet003002013
  Base = -> Fillet003002012
  Edges = 1 edges r=30: [Edge3]
FEATURE [Part::Fillet] Fillet003002014
  Base = -> Fillet003002013
  Edges = 1 edges r=30: [Edge17]
FEATURE [Part::Fillet] Fillet003002015
  Base = -> Fillet003002014
  Edges = 1 edges r=30: [Edge15]
